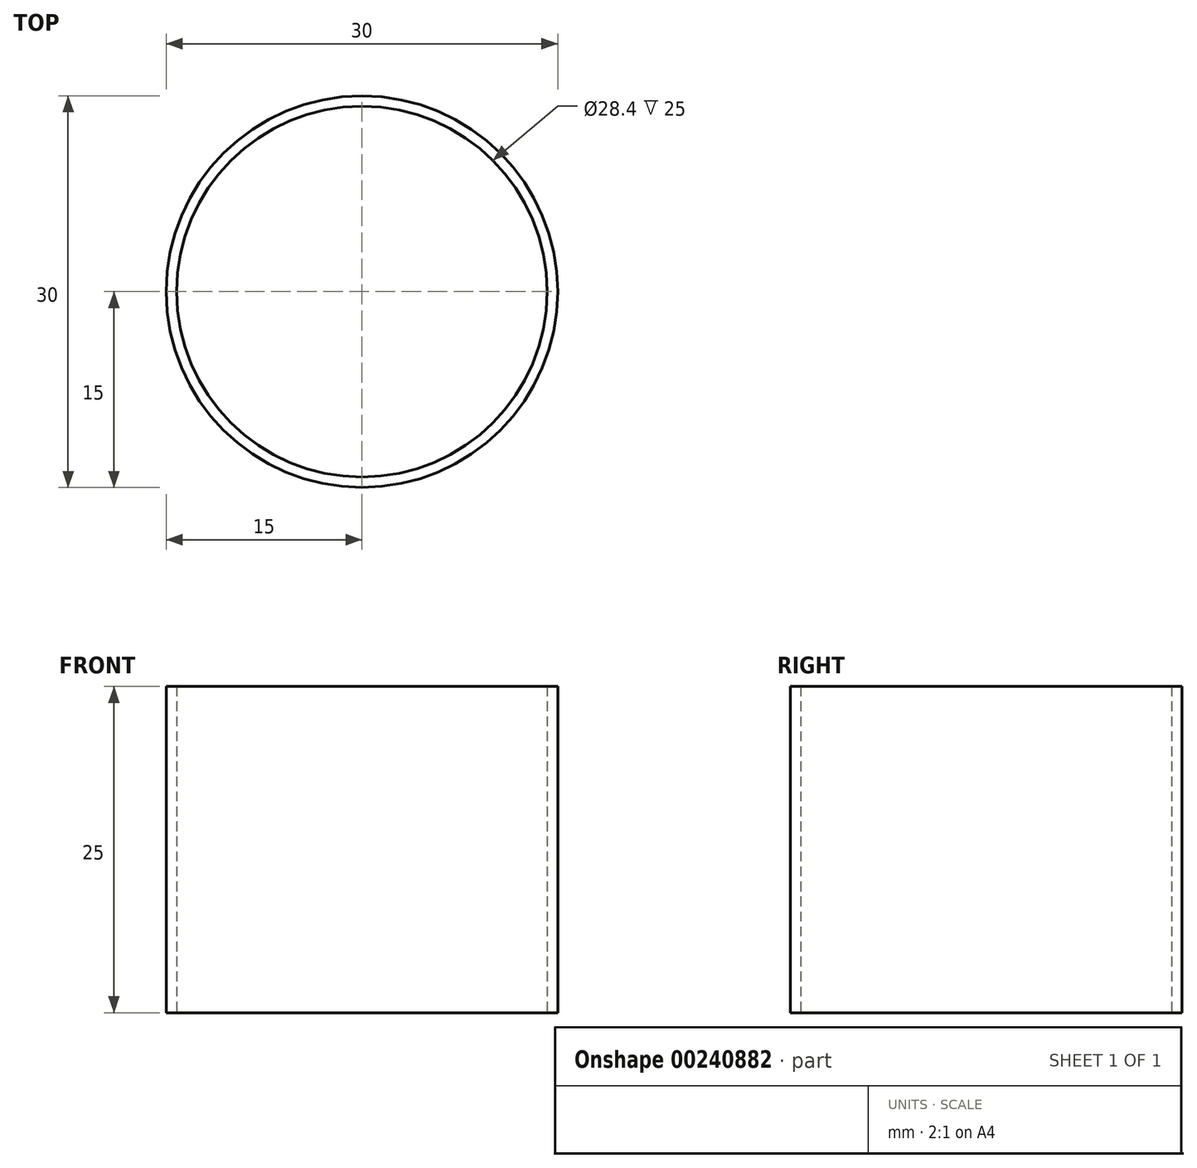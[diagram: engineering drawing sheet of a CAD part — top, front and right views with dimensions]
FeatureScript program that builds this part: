
annotation { "Feature Type Name" : "Feature", "Feature Type Description" : "" }
export const myFeature = defineFeature(function(context is Context, id is Id, definition is map)
    precondition{}
    {
        {
            var Q0;
            Q0=qCreatedBy(makeId("Top.planeOp"),FACE);
            var sketch = newSketch(context, id + "F0", { "sketchPlane" : qUnion([Q0])});
            skCircle(sketch, "E0", {"center": v(0, 0) * mm, "radius": 15 * mm});
            skCircle(sketch, "E1", {"center": v(0, 0) * mm, "radius": 14.2 * mm});
            skSolve(sketch);
        }
        {
            var Q0;
            Q0=makeQuery(id+"F0.imprint","IMPRINT",FACE,{"disambiguationData":[TD([[makeQuery(id+"F0.imprint","IMPRINT",EDGE,{"derivedFrom":sQuery(id+"F0.wireOp",EDGE,"E0")}),1.0]])]});
            extrude(context, id + "F1", {"entities" : qUnion([Q0]), "depth" : 25 * mm});
        }
    });
